# Revit family: 0041730
name_source: partatom
category: Lighting Fixtures
revit_build: Autodesk Revit 2017 (Build: 20190507_1515(x64)
units: mm (PartAtom-declared; Revit-internal decimal feet)

## family parameters
Cut with Voids When Loaded = No
Host = Face
Light Source = Yes
OmniClass Number = 23.80.70.00
OmniClass Title = Lighting
Part Type = Normal
Room Calculation Point = No
Round Connector Dimension = Use Diameter
Shared = No

## types (2) — shared parameters
Apparent Load = 2 VA
Assembly Code = D5020200
ClassificationName = Uniclass2015
ClassificationValue = EF_70_80
Color Filter = 16777215
Default Elevation = 1219 mm
Description = SylSafe Spot RA C EM3 NM DA is a miniature emergency surface mounted downlight with interchangeable optics for open area and escape route illumination. Non-maintained 3 hr emergency duration with NiMH rechargeable battery. Recharge period 24 hours. Self testing with DALI monitoring capability. 145lm, 1.8W, IK03, IP40. Power Factor 0.44. Class II electrical construction.
Dimming Lamp Color Temperature Shift = <None>
DimmingControlOptions = Non dimmable
DocumentationLiterature = https://www.sylvania-lighting.com
ElectricShockClassification = Class II
Emit Shape Visible in Rendering = No
Emit from Circle Diameter = 20 mm  [stored 0.0656168 ft]
IfcExportAs = IfcLightFixtureType
IfcExportType = IfcLightFixtureType
ImpactProtectionIndex = IK03
IngressProtection = IP40
InputNominalFrequency = 50/60Hz
InputVoltage = 230-240V~
Keynote = 16500
LampColourRenderingIndex = 70
LampColourTemperature = 6300
LampNominalLuminous = 145 lm
LuminousEfficacy = 81 lm/W
Manufacturer = Feilo Sylvania
ManufacturerName = Feilo Sylvania
Material_1_SYL = PC/ABS Plastic
Material_2_SYL = PC/ABS Plastic Transparent
Material_3_SYL = <By Category>
Material_4_SYL = <By Category>
Model = SYLSAFE SPOT RA C EM3 NM DA
ModelNumber = 0041730
ModelReference = SYLSAFE SPOT RA C EM3 NM DA
Name = SYLSAFE SPOT RA C EM3 NM DA
NominalDepth = 120 mm  [stored 0.393701 ft]
NominalHeight = 44 mm  [stored 0.144357 ft]
NominalLength = 120 mm  [stored 0.393701 ft]
PowerConsumption = 1.8 W
PowerFactor = 0.44
Tilt Angle = -90.00°
Type Image = <None>
TypeName = SYLSAFE SPOT RA C EM3 NM DA
URL = http://www.sylvania-lighting.com
Voltage = 230 V
Weight = 0.246 kg
zero-valued in all types: Cost

## per-type parameters (varying)
| type | Photometric Web File |
| SYLSAFE SPOT RA C EM3 NM DA - Escape Route | 0041730ER.ies |
| SYLSAFE SPOT RA C EM3 NM DA - Open Area | 0041730OA.ies |

note: [stored X ft] marks values corroborated as IEEE doubles in the binary element streams (Revit-internal decimal feet)

## geometry (parser evidence)
native form markers: Sweep x2
no freeform markers — native parametric forms only
